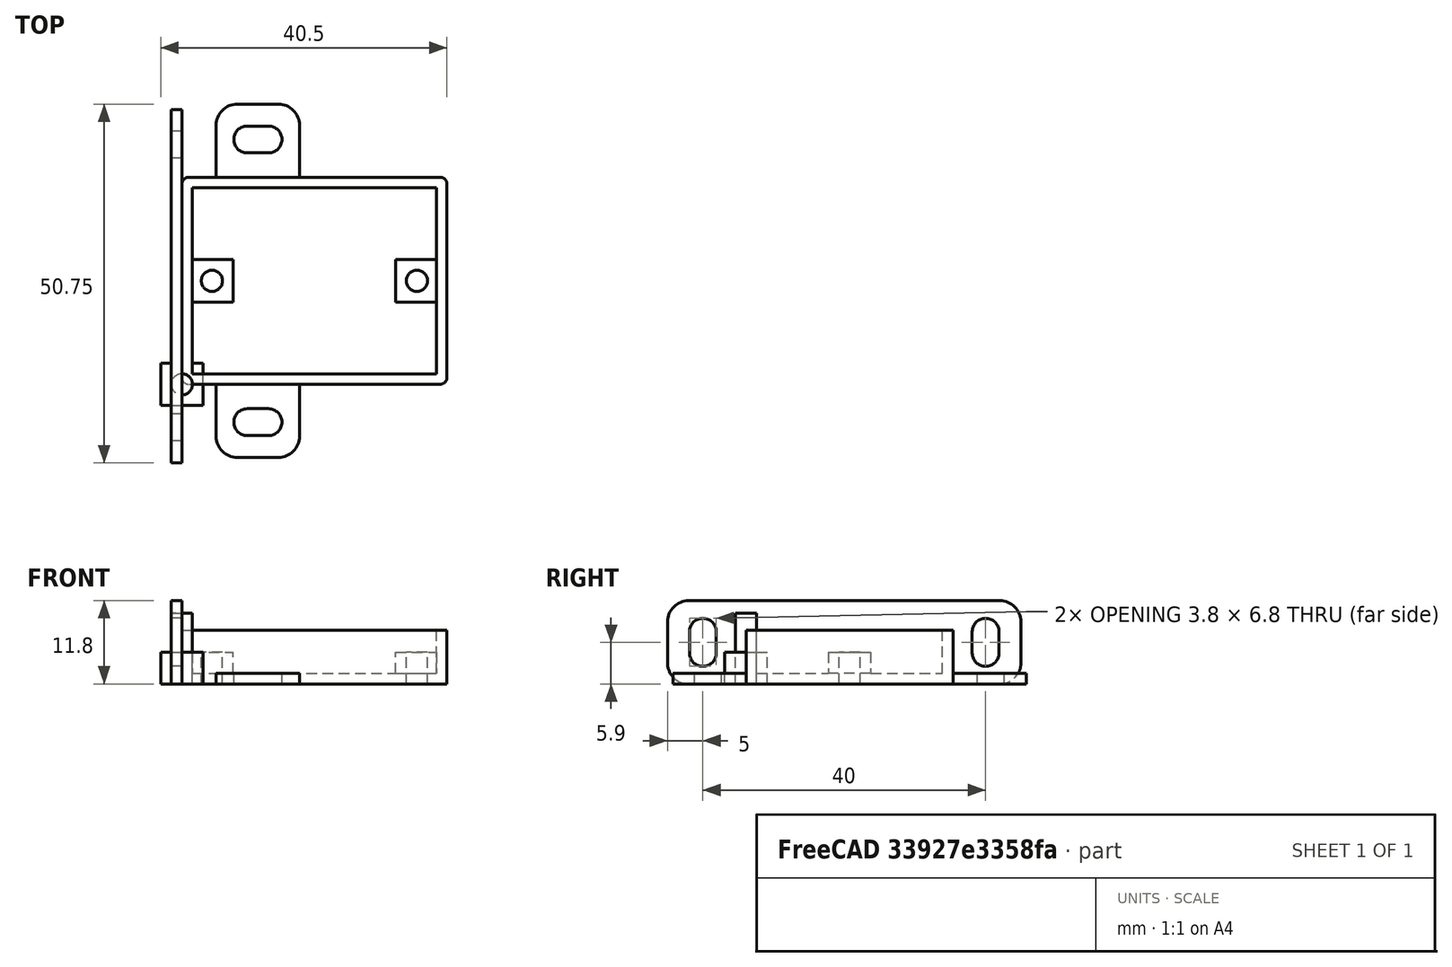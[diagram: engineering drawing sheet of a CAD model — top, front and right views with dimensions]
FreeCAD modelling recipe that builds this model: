
FCSTD DOCUMENT  (FreeCAD 0.19R23578 (Git))
Label: mosfet_keyes
License: FreeArt
LicenseURL: http://artlibre.org/licence/lal
objects: Part::Box×3, Part::FeaturePython×2, Part::Feature×2, Part::MultiFuse×2, Part::Cut×2, Spreadsheet::Sheet×1, Part::Fillet×1, Part::Cylinder×1, App::Part×1
note: 11 computed .brp shape members not serialized (recipe doc carries the construction recipe); baked Part::Feature solids carry a one-line shape summary decoded from their .brp

FEATURE [Spreadsheet::Sheet] Spreadsheet  label="p"
  cells = A1=pcb_x; B1(pcb_x)=34.5; A2=pcb_y; B2(pcb_y)=26.3; A3=pcb_z; B3(pcb_z)=1.6; A4=pcb_under; B4(pcb_under)=3; A5=side_wall; B5(side_wall)=1.5; A6=bottom_wall; B6(bottom_wall)=1.5; A7=pcb_above; B7(pcb_above)=1.5; A8=hole_dist_x; B8(hole_dist_x)=29; A9=hole_r; B9(hole_r)=1.5; A10=hole_off_y; B10(hole_off_y)==pcb_y / 2; A11=hole_stand_size; B11(hole_stand_size)=6
FEATURE [Part::Box] Box  label="external cube"
  AttacherType = Attacher::AttachEngine3D
  Height = 7.6
  Length = 37.5
  Width = 29.3
  expr: Height = <<p>>.bottom_wall + <<p>>.pcb_under + <<p>>.pcb_z + <<p>>.pcb_above
  expr: Width = <<p>>.pcb_y + 2 * <<p>>.side_wall
  expr: Length = <<p>>.pcb_x + 2 * <<p>>.side_wall
FEATURE [Part::Box] Box006  label="internal cube"
  AttacherType = Attacher::AttachEngine3D
  Height = 6.1
  Length = 34.5
  Placement = pos=(1.5,1.5,1.5) rot=(0,0,1;0rad)
  Width = 26.3
  expr: .Placement.Base.y = <<p>>.side_wall
  expr: .Placement.Base.x = <<p>>.side_wall
  expr: .Placement.Base.z = <<p>>.bottom_wall
  expr: Height = <<p>>.pcb_under + <<p>>.pcb_z + <<p>>.pcb_above
  expr: Width = <<p>>.pcb_y
  expr: Length = <<p>>.pcb_x
FEATURE [Part::Fillet] Fillet  label="external fillet"
  Base = -> Box
  Edges = 4 edges r=1: [Edge1,Edge3,Edge5,Edge7]
FEATURE [Part::Cylinder] Cylinder  label="hole"
  Angle = 360
  AttacherType = Attacher::AttachEngine3D
  Height = 10
  Radius = 1.5
  expr: Radius = <<p>>.hole_r
FEATURE [Part::Box] Box008  label="stand"
  AttacherType = Attacher::AttachEngine3D
  Height = 4.5
  Length = 6
  Placement = pos=(-3,-3,0) rot=(0,0,1;0rad)
  Width = 6
  expr: Height = <<p>>.pcb_under + <<p>>.bottom_wall
  expr: Length = <<p>>.hole_stand_size
  expr: Width = <<p>>.hole_stand_size
  expr: .Placement.Base.x = -<<p>>.hole_stand_size / 2
  expr: .Placement.Base.y = -<<p>>.hole_stand_size / 2
FEATURE [Part::FeaturePython] Array  label="hole array"  # Draft array (typed FeaturePython)
  Angle = 360
  ArrayType = 0
  Axis = (0,0,1)
  Base = -> Box008
  Center = (0,0,0)
  Count = 2
  ExpandArray = false
  Fuse = false
  IntervalAxis = (0,0,0)
  IntervalX = (29,0,0)
  IntervalY = (0,1,0)
  IntervalZ = (0,0,100)
  NumberCircles = 3
  NumberPolar = 5
  NumberX = 2
  NumberY = 1
  NumberZ = 1
  Placement = pos=(4.25,14.65,0) rot=(0,0,1;0rad)
  PlacementList = 2 placements: [(-3,-3,0),(26,-3,0)]
  RadialDistance = 50
  ScaleList = (2) [(1,1,1),(1,1,1)]
  Symmetry = 1
  TangentialDistance = 25
  expr: .Placement.Base.y = Spreadsheet.hole_off_y + <<p>>.side_wall
  expr: .Placement.Base.x = (2 * <<p>>.side_wall + <<p>>.pcb_x - Spreadsheet.hole_dist_x) / 2
  expr: .IntervalX.x = Spreadsheet.hole_dist_x
FEATURE [Part::FeaturePython] Array001  label="hole array001"  # Draft array (typed FeaturePython)
  Angle = 360
  ArrayType = 0
  Axis = (0,0,1)
  Base = -> Cylinder
  Center = (0,0,0)
  Count = 2
  ExpandArray = false
  Fuse = false
  IntervalAxis = (0,0,0)
  IntervalX = (29,0,0)
  IntervalY = (0,1,0)
  IntervalZ = (0,0,100)
  NumberCircles = 3
  NumberPolar = 5
  NumberX = 2
  NumberY = 1
  NumberZ = 1
  Placement = pos=(4.25,14.65,0) rot=(0,0,1;0rad)
  PlacementList = 2 placements: [(0,0,0),(29,0,0)]
  RadialDistance = 50
  ScaleList = (2) [(1,1,1),(1,1,1)]
  Symmetry = 1
  TangentialDistance = 25
  expr: .IntervalX.x = Spreadsheet.hole_dist_x
  expr: .Placement.Base.x = (2 * <<p>>.side_wall + <<p>>.pcb_x - Spreadsheet.hole_dist_x) / 2
  expr: .Placement.Base.y = Spreadsheet.hole_off_y + <<p>>.side_wall
FEATURE [Part::Feature] Body001001  label="attach plane y rotated dir001"
  Placement = pos=(0,-11.1,0) rot=(0,-1,0;1.5708rad)
  shape: bbox 1.5 x 50 x 11.8 mm, 20 faces (baked)
FEATURE [Part::Feature] Cut002001  label="attach plane y dir001"
  Placement = pos=(4.85,-10.35,0) rot=(0,0,1;0rad)
  shape: bbox 11.8 x 50 x 1.5 mm, 20 faces (baked)
FEATURE [Part::MultiFuse] Fusion001  label="body fusion"
  Shapes = -> [Fillet,Cut002001]
FEATURE [Part::Cut] Cut  label="body cut"
  Base = -> Fusion001
  Tool = -> Box006
FEATURE [Part::MultiFuse] Fusion002  label="mosfet fusion"
  Shapes = -> [Array,Cut]
FEATURE [Part::Cut] Cut003003  label="mosfet cut"
  Base = -> Fusion002
  Tool = -> Array001
FEATURE [App::Part] Part  label="mosfet pcb box part"
  Group = -> [Box,Fillet,Fusion001,Box006,Cut,Cylinder,Box008,Array,Fusion002,Array001,Cut003003]
  Origin = -> Origin
